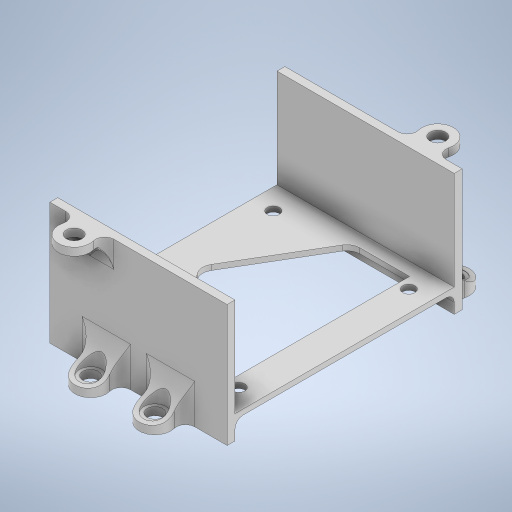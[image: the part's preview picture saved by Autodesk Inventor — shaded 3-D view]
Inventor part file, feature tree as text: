
AUTODESK INVENTOR PART (.ipt)
format: ipt  version: 2024 (Build 280153000, 153)  size: 951,296 bytes
history: native  units: in
note: dims shown in document units (in); Inventor stores cm internally (conversion verified against a paired STEP export)
features: extrude x9, fillet x5, sketch x3, plane x1, projected_geometry x1
ambient origin geometry x8: Origin, YZ Plane, XZ Plane, XY Plane, X Axis, Y Axis, Z Axis, Center Point
bodies: Solid1 (feature_tree)
feature tree (19):
  extrude  "Extrusion1"  Depth=0.1181in
  extrude  "Extrusion2"  Depth=0.1969in
  extrude  "Extrusion6"  Depth=0.4724in
  extrude  "Extrusion7"  Depth=0.4724in
  extrude  "Extrusion8"  Depth=2.6575in
  plane  "Work Plane1"
  extrude  "Extrusion9"  Depth=1.3287in
  fillet  "Fillet2"  Radius=1.6437in
  fillet  "Fillet7"  Radius=0.0787in
  extrude  "Extrusion10"  Depth=1.5551in TaperAngle=0.0deg
  extrude  "Extrusion11"  Depth=0.185in
  extrude  "Extrusion12"  Depth=0.313in
  fillet  "Fillet8"  Radius=0.313in
  fillet  "Fillet9"  Radius=0.1181in
  fillet  "Fillet10"  Radius=0.2362in
  sketch  "Sketch9"  dims[d0=3.2874in d1=0.1181in]
  sketch  "Sketch10"  dims[d2=0.1181in d4=0.1969in]
  sketch  "Sketch11"  dims[d5=0.1969in d6=0.4724in d7=0.4724in d8=2.6575in d9=1.3287in d10=1.6437in d11=0.0787in d12=0.0in d13=1.5551in d14=0.2756in d15=0.0in d16=0.0in d35=0.185in d36=0.313in d38=0.313in d40=0.1181in d41=0.0in d46=0.2362in d47=0.2362in d48=0.2362in d49=0.2362in d51=0.4724in d54=0.1378in d55=0.9646in d56=1.9291in d57=0.4823in d58=0.9646in d59=0.5906in d60=0.0in d61=0.3346in d62=0.3346in d63=0.3346in d64=0.3346in d65=0.4724in d66=0.0in d67=1.1811in d68=0.1181in d69=0.1969in d70=0.0in d72=0.3346in d73=2.5512in d74=1.2756in d75=2.7559in d76=0.0in d77=0.1969in d80=0.1181in d85=0.1181in d87=0.0662in d90=0.2362in d91=0.4724in d92=0.2756in d93=1.4567in d94=2.6575in d95=0.6004in d96=0.3937in d97=0.0in d100=0.4724in d102=0.2756in d103=0.0in d105=0.1181in d106=0.315in d107=0.315in d108=0.1181in d111=0.0in d112=0.0in d113=0.0591in d114=0.0197in d115=0.0118in d31=0.0197in d32=0.0344in d33=0.0197in d34=0.0344in]
  projected_geometry  "Projected Loop3"
